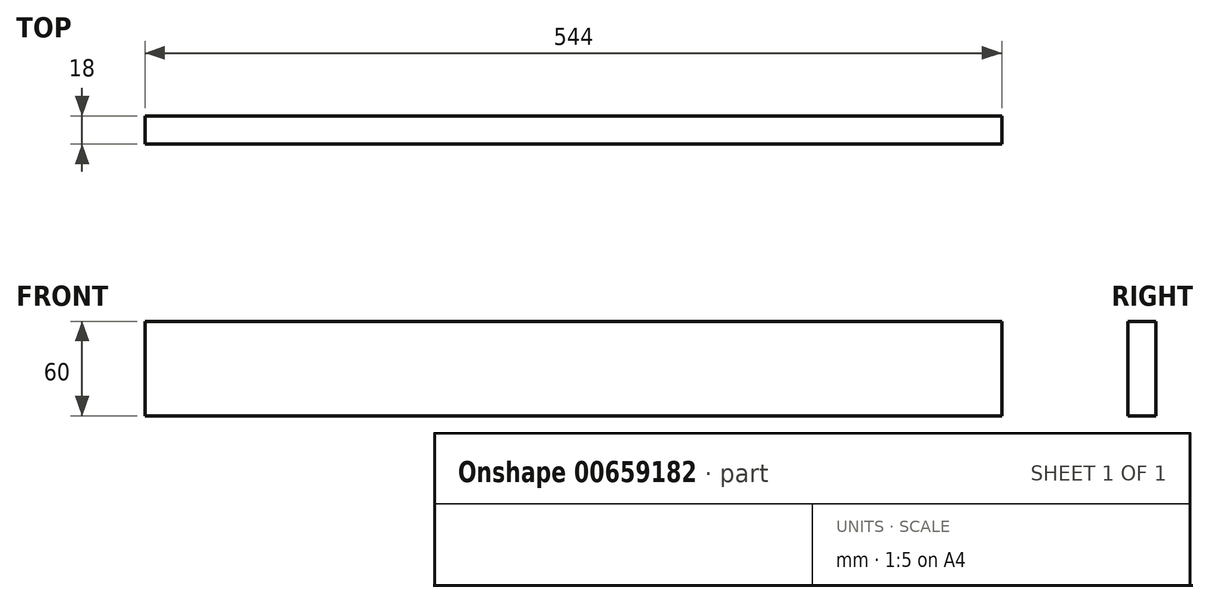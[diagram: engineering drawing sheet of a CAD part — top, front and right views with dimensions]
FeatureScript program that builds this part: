
annotation { "Feature Type Name" : "Feature", "Feature Type Description" : "" }
export const myFeature = defineFeature(function(context is Context, id is Id, definition is map)
    precondition{}
    {
        {
            var Q0;
            Q0=qCreatedBy(makeId("Front.planeOp"),FACE);
            var sketch = newSketch(context, id + "F0", { "sketchPlane" : qUnion([Q0])});
            skLineSegment(sketch, "E0.bottom", {"start": v(-272, -30) * mm, "end": v(272, -30) * mm});
            skLineSegment(sketch, "E0.top", {"start": v(-272, 30) * mm, "end": v(272, 30) * mm});
            skLineSegment(sketch, "E0.left", {"start": v(-272, -30) * mm, "end": v(-272, 30) * mm});
            skLineSegment(sketch, "E0.right", {"start": v(272, -30) * mm, "end": v(272, 30) * mm});
            skPoint(sketch, "E0.middle", {"position": v(0, 0) * mm});
            skSolve(sketch);
        }
        {
            var Q0;
            Q0=makeQuery(id+"F0.imprint","IMPRINT",FACE,{"disambiguationData":[TD([[makeQuery(id+"F0.imprint","IMPRINT",EDGE,{"derivedFrom":sQuery(id+"F0.wireOp",EDGE,"E0.bottom")}),1.0]])]});
            extrude(context, id + "F1", {"entities" : qUnion([Q0]), "endBound" : BoundingType.SYMMETRIC, "depth" : 18 * mm, "offsetDistance" : 25 * mm});
        }
    });
